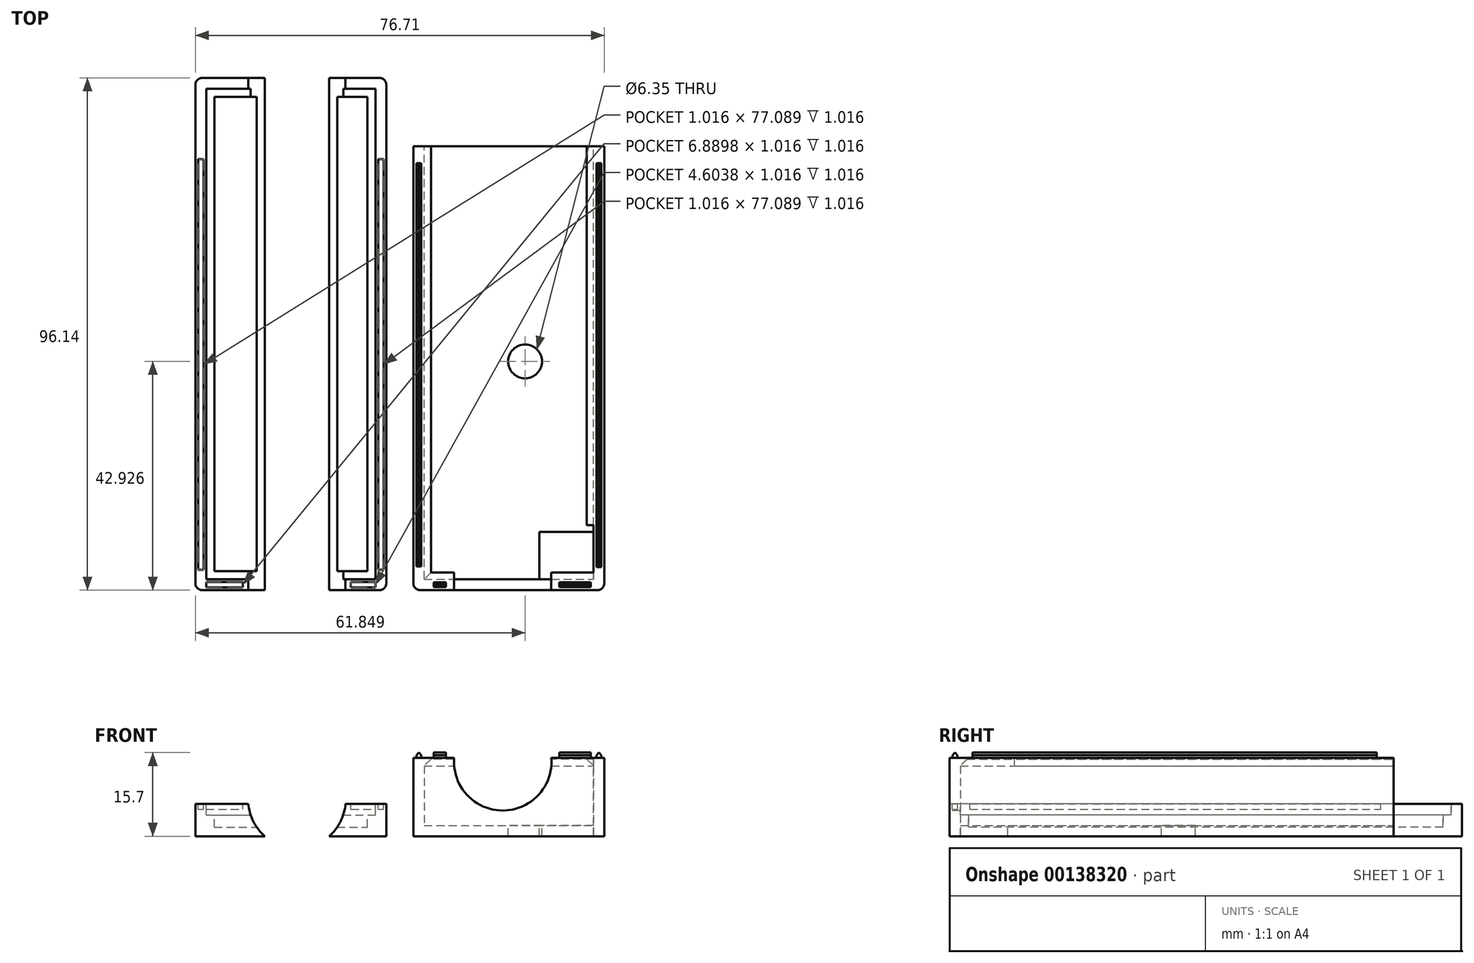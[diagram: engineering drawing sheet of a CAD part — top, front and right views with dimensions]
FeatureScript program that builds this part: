
annotation { "Feature Type Name" : "Feature", "Feature Type Description" : "" }
export const myFeature = defineFeature(function(context is Context, id is Id, definition is map)
    precondition{}
    {
        {
            var Q0;
            Q0=qCreatedBy(makeId("Top.planeOp"),FACE);
            var sketch = newSketch(context, id + "F0", { "sketchPlane" : qUnion([Q0])});
            skLineSegment(sketch, "E0.bottom", {"start": v(2.54, 98.68) * mm, "end": v(38.35, 98.68) * mm});
            skLineSegment(sketch, "E0.top", {"start": v(2.54, 2.54) * mm, "end": v(38.35, 2.54) * mm});
            skLineSegment(sketch, "E0.left", {"start": v(2.54, 98.68) * mm, "end": v(2.54, 2.54) * mm});
            skLineSegment(sketch, "E0.right", {"start": v(38.35, 98.68) * mm, "end": v(38.35, 2.54) * mm});
            skSolve(sketch);
        }
        {
            var Q0;
            Q0 = qSketchRegion(id + "F0", true);
            extrude(context, id + "F1", {"entities" : qUnion([Q0]), "depth" : 6.1 * mm, "offsetDistance" : 25.4 * mm});
        }
        {
            var Q0;
            Q0=makeQuery(id+"F1.opExtrude","CAP_FACE",FACE,{"disambiguationData":[OSD([sQuery(id+"F0.wireOp",EDGE,"E0.bottom"),sQuery(id+"F0.wireOp",EDGE,"E0.top"),sQuery(id+"F0.wireOp",EDGE,"E0.left"),sQuery(id+"F0.wireOp",EDGE,"E0.right")])],"isStart":false});
            var sketch = newSketch(context, id + "F2", { "sketchPlane" : qUnion([Q0])});
            skLineSegment(sketch, "E1.0", {"start": v(34.8, 95.12) * mm, "end": v(34.8, 6.1) * mm});
            skLineSegment(sketch, "E1.1", {"start": v(6.1, 95.12) * mm, "end": v(34.8, 95.12) * mm});
            skLineSegment(sketch, "E1.2", {"start": v(6.1, 95.12) * mm, "end": v(6.1, 6.1) * mm});
            skLineSegment(sketch, "E1.3", {"start": v(6.1, 6.1) * mm, "end": v(34.8, 6.1) * mm});
            skSolve(sketch);
        }
        {
            var Q0;
            Q0 = qSketchRegion(id + "F2", true);
            extrude(context, id + "F3", {"entities" : qUnion([Q0]), "operationType" : NewBodyOperationType.REMOVE, "oppositeDirection" : true, "depth" : 4.4 * mm, "offsetDistance" : 25.4 * mm});
        }
        {
            var Q0;
            Q0=makeQuery(id+"F1.opExtrude","CAP_FACE",FACE,{"disambiguationData":[OSD([sQuery(id+"F0.wireOp",EDGE,"E0.bottom"),sQuery(id+"F0.wireOp",EDGE,"E0.top"),sQuery(id+"F0.wireOp",EDGE,"E0.left"),sQuery(id+"F0.wireOp",EDGE,"E0.right")])],"isStart":false});
            var sketch = newSketch(context, id + "F4", { "sketchPlane" : qUnion([Q0])});
            skLineSegment(sketch, "E2.0", {"start": v(4.57, 96.65) * mm, "end": v(4.57, 4.57) * mm});
            skLineSegment(sketch, "E2.1", {"start": v(4.57, 96.65) * mm, "end": v(36.32, 96.65) * mm});
            skLineSegment(sketch, "E2.2", {"start": v(36.32, 96.65) * mm, "end": v(36.32, 4.57) * mm});
            skLineSegment(sketch, "E2.3", {"start": v(4.57, 4.57) * mm, "end": v(36.32, 4.57) * mm});
            skLineSegment(sketch, "E3.bottom", {"start": v(6.1, 6.1) * mm, "end": v(34.8, 6.1) * mm});
            skLineSegment(sketch, "E3.top", {"start": v(6.1, 95.12) * mm, "end": v(34.8, 95.12) * mm});
            skLineSegment(sketch, "E3.left", {"start": v(6.1, 6.1) * mm, "end": v(6.1, 95.12) * mm});
            skLineSegment(sketch, "E3.right", {"start": v(34.8, 6.1) * mm, "end": v(34.8, 95.12) * mm});
            skSolve(sketch);
        }
        {
            var Q0;
            Q0 = qSketchRegion(id + "F4", true);
            extrude(context, id + "F5", {"entities" : qUnion([Q0]), "operationType" : NewBodyOperationType.REMOVE, "oppositeDirection" : true, "depth" : 2.1 * mm, "offsetDistance" : 25.4 * mm});
        }
        {
            var Q0;
            Q0=qCreatedBy(makeId("Top.planeOp"),FACE);
            var sketch = newSketch(context, id + "F6", { "sketchPlane" : qUnion([Q0])});
            skLineSegment(sketch, "E4.bottom", {"start": v(43.43, 2.54) * mm, "end": v(79.25, 2.54) * mm});
            skLineSegment(sketch, "E4.top", {"start": v(43.43, 98.55) * mm, "end": v(79.25, 98.55) * mm});
            skLineSegment(sketch, "E4.left", {"start": v(43.43, 2.54) * mm, "end": v(43.43, 98.55) * mm});
            skLineSegment(sketch, "E4.right", {"start": v(79.25, 2.54) * mm, "end": v(79.25, 98.55) * mm});
            skSolve(sketch);
        }
        {
            var Q0;
            Q0 = qSketchRegion(id + "F6", true);
            extrude(context, id + "F7", {"entities" : qUnion([Q0]), "depth" : 14.73 * mm, "offsetDistance" : 25.4 * mm});
        }
        {
            var Q0;
            Q0=makeQuery(id+"F7.opExtrude","CAP_FACE",FACE,{"disambiguationData":[OSD([sQuery(id+"F6.wireOp",EDGE,"E4.bottom"),sQuery(id+"F6.wireOp",EDGE,"E4.top"),sQuery(id+"F6.wireOp",EDGE,"E4.left"),sQuery(id+"F6.wireOp",EDGE,"E4.right")])],"isStart":false});
            shell(context, id + "F8", {"entities" : qUnion([Q0]), "thickness" : 2.03 * mm});
        }
        {
            var Q0;
            Q0=makeQuery(id+"F7.opExtrude","CAP_FACE",FACE,{"disambiguationData":[OSD([sQuery(id+"F6.wireOp",EDGE,"E4.bottom"),sQuery(id+"F6.wireOp",EDGE,"E4.top"),sQuery(id+"F6.wireOp",EDGE,"E4.left"),sQuery(id+"F6.wireOp",EDGE,"E4.right")])],"isStart":false});
            var sketch = newSketch(context, id + "F9", { "sketchPlane" : qUnion([Q0])});
            skLineSegment(sketch, "E5.bottom", {"start": v(43.43, 98.55) * mm, "end": v(79.25, 98.55) * mm});
            skLineSegment(sketch, "E5.top", {"start": v(43.43, 85.85) * mm, "end": v(79.25, 85.85) * mm});
            skLineSegment(sketch, "E5.left", {"start": v(43.43, 98.55) * mm, "end": v(43.43, 85.85) * mm});
            skLineSegment(sketch, "E5.right", {"start": v(79.25, 98.55) * mm, "end": v(79.25, 85.85) * mm});
            skLineSegment(sketch, "E6.bottom", {"start": v(77.22, 4.57) * mm, "end": v(67.06, 4.57) * mm});
            skLineSegment(sketch, "E6.top", {"start": v(77.22, 13.46) * mm, "end": v(67.06, 13.46) * mm});
            skLineSegment(sketch, "E6.left", {"start": v(77.22, 4.57) * mm, "end": v(77.22, 13.46) * mm});
            skLineSegment(sketch, "E6.right", {"start": v(67.06, 4.57) * mm, "end": v(67.06, 13.46) * mm});
            skCircle(sketch, "E7", {"center": v(64.39, 45.47) * mm, "radius": 3.18 * mm});
            skSolve(sketch);
        }
        {
            var Q0;
            Q0 = qSketchRegion(id + "F9", true);
            extrude(context, id + "F10", {"entities" : qUnion([Q0]), "operationType" : NewBodyOperationType.REMOVE, "endBound" : BoundingType.THROUGH_ALL, "oppositeDirection" : true, "depth" : 25.4 * mm, "offsetDistance" : 25.4 * mm});
        }
        {
            var Q0;
            {var subQ0=sQuery(id+"F6.wireOp",EDGE,"E4.bottom");var subQ1=sQuery(id+"F6.wireOp",EDGE,"E4.right");Q0=makeQuery(id+"F10.boolean.opBoolean","SPLIT",FACE,{"disambiguationData":[TD([makeQuery(id+"F7.opExtrude","SWEPT_FACE",FACE,{"disambiguationData":[OSD([subQ1])]})])],"derivedFrom":makeQuery(id+"F7.opExtrude","CAP_FACE",FACE,{"disambiguationData":[OSD([subQ0,sQuery(id+"F6.wireOp",EDGE,"E4.top"),sQuery(id+"F6.wireOp",EDGE,"E4.left"),subQ1])],"isStart":false})});}
            var sketch = newSketch(context, id + "F11", { "sketchPlane" : qUnion([Q0])});
            skLineSegment(sketch, "E8.bottom", {"start": v(77.22, 14.73) * mm, "end": v(75.95, 14.73) * mm});
            skLineSegment(sketch, "E8.top", {"start": v(77.22, 85.85) * mm, "end": v(75.95, 85.85) * mm});
            skLineSegment(sketch, "E8.left", {"start": v(77.22, 14.73) * mm, "end": v(77.22, 85.85) * mm});
            skLineSegment(sketch, "E8.right", {"start": v(75.95, 14.73) * mm, "end": v(75.95, 85.85) * mm});
            skLineSegment(sketch, "E9.bottom", {"start": v(45.47, 4.57) * mm, "end": v(77.22, 4.57) * mm});
            skLineSegment(sketch, "E9.top", {"start": v(46.74, 5.84) * mm, "end": v(77.22, 5.84) * mm});
            skLineSegment(sketch, "E9.right", {"start": v(77.22, 4.57) * mm, "end": v(77.22, 5.84) * mm});
            skLineSegment(sketch, "E10.top", {"start": v(46.74, 85.85) * mm, "end": v(45.47, 85.85) * mm});
            skLineSegment(sketch, "E10.left", {"start": v(46.74, 5.84) * mm, "end": v(46.74, 85.85) * mm});
            skLineSegment(sketch, "E10.right", {"start": v(45.47, 4.57) * mm, "end": v(45.47, 85.85) * mm});
            skSolve(sketch);
        }
        {
            var Q0;
            Q0 = qSketchRegion(id + "F11", true);
            extrude(context, id + "F12", {"entities" : qUnion([Q0]), "operationType" : NewBodyOperationType.ADD, "oppositeDirection" : true, "depth" : 1.52 * mm, "offsetDistance" : 25.4 * mm});
        }
        {
            var Q0;
            Q0=makeQuery(id+"F12.opExtrude","CAP_EDGE",EDGE,{"disambiguationData":[OSD([sQuery(id+"F11.wireOp",EDGE,"E9.top")])],"isStart":false});
            var Q1;
            Q1=makeQuery(id+"F12.opExtrude","CAP_EDGE",EDGE,{"disambiguationData":[OSD([sQuery(id+"F11.wireOp",EDGE,"E8.right")])],"isStart":false});
            var Q2;
            Q2=makeQuery(id+"F12.opExtrude","CAP_EDGE",EDGE,{"disambiguationData":[OSD([sQuery(id+"F11.wireOp",EDGE,"E10.left")])],"isStart":false});
            var Q3;
            Q3=makeQuery(id+"F12.opExtrude","CAP_EDGE",EDGE,{"disambiguationData":[OSD([sQuery(id+"F11.wireOp",EDGE,"Zw6snLi4-Jf5f-Ahn4-wR1g-vWgNg3NE2vRn.top")])],"isStart":false});
            chamfer(context, id + "F13", {"entities" : qUnion([Q0, Q1, Q2, Q3]), "width" : 1.27 * mm, "tangentPropagation" : true});
        }
        {
            var Q0;
            Q0=makeQuery(id+"F7.opExtrude","SWEPT_EDGE",EDGE,{"disambiguationData":[OSD([sQuery(id+"F6.wireOp",EDGE,"E4.bottom"),sQuery(id+"F6.wireOp",EDGE,"E4.right")])]});
            var Q1;
            Q1=makeQuery(id+"F7.opExtrude","SWEPT_EDGE",EDGE,{"disambiguationData":[OSD([sQuery(id+"F6.wireOp",EDGE,"E4.bottom"),sQuery(id+"F6.wireOp",EDGE,"E4.left")])]});
            var Q2;
            Q2=makeQuery(id+"F1.opExtrude","SWEPT_EDGE",EDGE,{"disambiguationData":[OSD([sQuery(id+"F0.wireOp",EDGE,"E0.top"),sQuery(id+"F0.wireOp",EDGE,"E0.right")])]});
            var Q3;
            Q3=makeQuery(id+"F1.opExtrude","SWEPT_EDGE",EDGE,{"disambiguationData":[OSD([sQuery(id+"F0.wireOp",EDGE,"E0.bottom"),sQuery(id+"F0.wireOp",EDGE,"E0.right")])]});
            var Q4;
            Q4=makeQuery(id+"F1.opExtrude","SWEPT_EDGE",EDGE,{"disambiguationData":[OSD([sQuery(id+"F0.wireOp",EDGE,"E0.top"),sQuery(id+"F0.wireOp",EDGE,"E0.left")])]});
            var Q5;
            Q5=makeQuery(id+"F1.opExtrude","SWEPT_EDGE",EDGE,{"disambiguationData":[OSD([sQuery(id+"F0.wireOp",EDGE,"E0.bottom"),sQuery(id+"F0.wireOp",EDGE,"E0.left")])]});
            fillet(context, id + "F14", {"entities" : qUnion([Q0, Q1, Q2, Q3, Q4, Q5]), "tangentPropagation" : true, "radius" : 1.27 * mm, "defaultsChanged" : false, "vertexSettings" : [], "allowEdgeOverflow" : false});
        }
        {
            var Q0;
            Q0=makeQuery(id+"F7.opExtrude","SWEPT_FACE",FACE,{"disambiguationData":[OSD([sQuery(id+"F6.wireOp",EDGE,"E4.bottom")])]});
            var sketch = newSketch(context, id + "F15", { "sketchPlane" : qUnion([Q0])});
            skCircle(sketch, "E11", {"center": v(60.2, 13.97) * mm, "radius": 9.14 * mm});
            skPoint(sketch, "E11.centerSnap0", {"position": v(61.34, 14.73) * mm});
            skCircle(sketch, "E12", {"center": v(21.59, 6.86) * mm, "radius": 9.14 * mm});
            skSolve(sketch);
        }
        {
            var Q0;
            Q0 = qSketchRegion(id + "F15", true);
            extrude(context, id + "F16", {"entities" : qUnion([Q0]), "operationType" : NewBodyOperationType.REMOVE, "endBound" : BoundingType.THROUGH_ALL, "oppositeDirection" : true, "depth" : 25.4 * mm, "offsetDistance" : 25.4 * mm});
        }
        {
            var Q0;
            Q0 = qSketchRegion(id + "F15", true);
            extrude(context, id + "F17", {"entities" : qUnion([Q0]), "operationType" : NewBodyOperationType.REMOVE, "oppositeDirection" : true, "depth" : 3.56 * mm, "offsetDistance" : 25.4 * mm});
        }
        {
            var Q0;
            Q0=makeQuery(id+"F1.opExtrude","CAP_FACE",FACE,{"disambiguationData":[OSD([sQuery(id+"F0.wireOp",EDGE,"E0.bottom"),sQuery(id+"F0.wireOp",EDGE,"E0.top"),sQuery(id+"F0.wireOp",EDGE,"E0.left"),sQuery(id+"F0.wireOp",EDGE,"E0.right")])],"isStart":false});
            var sketch = newSketch(context, id + "F18", { "sketchPlane" : qUnion([Q0])});
            skLineSegment(sketch, "E13.bottom", {"start": v(4.57, 3.05) * mm, "end": v(11.46, 3.05) * mm});
            skLineSegment(sketch, "E13.top", {"start": v(4.57, 4.06) * mm, "end": v(11.46, 4.06) * mm});
            skLineSegment(sketch, "E13.left", {"start": v(4.57, 3.05) * mm, "end": v(4.57, 4.06) * mm});
            skLineSegment(sketch, "E13.right", {"start": v(11.46, 3.05) * mm, "end": v(11.46, 4.06) * mm});
            skLineSegment(sketch, "E14.bottom", {"start": v(3.05, 6.35) * mm, "end": v(4.06, 6.35) * mm});
            skLineSegment(sketch, "E14.top", {"start": v(3.05, 83.44) * mm, "end": v(4.06, 83.44) * mm});
            skLineSegment(sketch, "E14.left", {"start": v(3.05, 6.35) * mm, "end": v(3.05, 83.44) * mm});
            skLineSegment(sketch, "E14.right", {"start": v(4.06, 6.35) * mm, "end": v(4.06, 83.44) * mm});
            skLineSegment(sketch, "E15.bottom", {"start": v(36.83, 6.35) * mm, "end": v(37.85, 6.35) * mm});
            skLineSegment(sketch, "E15.top", {"start": v(36.83, 83.44) * mm, "end": v(37.85, 83.44) * mm});
            skLineSegment(sketch, "E15.left", {"start": v(36.83, 6.35) * mm, "end": v(36.83, 83.44) * mm});
            skLineSegment(sketch, "E15.right", {"start": v(37.85, 6.35) * mm, "end": v(37.85, 83.44) * mm});
            skLineSegment(sketch, "E16.bottom", {"start": v(31.72, 3.05) * mm, "end": v(36.32, 3.05) * mm});
            skLineSegment(sketch, "E16.top", {"start": v(31.72, 4.06) * mm, "end": v(36.32, 4.06) * mm});
            skLineSegment(sketch, "E16.left", {"start": v(31.72, 3.05) * mm, "end": v(31.72, 4.06) * mm});
            skLineSegment(sketch, "E16.right", {"start": v(36.32, 3.05) * mm, "end": v(36.32, 4.06) * mm});
            skSolve(sketch);
        }
        {
            var Q0;
            Q0 = qSketchRegion(id + "F18", true);
            extrude(context, id + "F19", {"entities" : qUnion([Q0]), "operationType" : NewBodyOperationType.REMOVE, "oppositeDirection" : true, "depth" : 1.02 * mm, "offsetDistance" : 25.4 * mm});
        }
        {
            var Q0;
            {var subQ0=sQuery(id+"F11.wireOp",EDGE,"E8.top");var subQ1=sQuery(id+"F6.wireOp",EDGE,"E4.bottom");var subQ2=sQuery(id+"F11.wireOp",EDGE,"E10.left");var subQ3=sQuery(id+"F6.wireOp",EDGE,"E4.left");var subQ4=sQuery(id+"F11.wireOp",EDGE,"E9.top");var subQ5=sQuery(id+"F11.wireOp",EDGE,"E10.top");Q0=makeQuery(id+"F16.boolean.opBoolean","SPLIT",FACE,{"disambiguationData":[TD([makeQuery(id+"F7.opExtrude","SWEPT_FACE",FACE,{"disambiguationData":[OSD([subQ3])]})])],"derivedFrom":makeQuery(id+"F12.boolean.opBoolean","MERGE",FACE,{"derivedFrom":[makeQuery(id+"F7.opExtrude","CAP_FACE",FACE,{"disambiguationData":[OSD([subQ1,sQuery(id+"F6.wireOp",EDGE,"E4.top"),subQ3,sQuery(id+"F6.wireOp",EDGE,"E4.right")])],"isStart":false}),makeQuery(id+"F12.opExtrude","CAP_FACE",FACE,{"disambiguationData":[OSD([sQuery(id+"F11.wireOp",EDGE,"E8.bottom"),subQ0,sQuery(id+"F11.wireOp",EDGE,"E8.left"),sQuery(id+"F11.wireOp",EDGE,"E8.right")])],"isStart":true}),makeQuery(id+"F12.opExtrude","CAP_FACE",FACE,{"disambiguationData":[OSD([sQuery(id+"F11.wireOp",EDGE,"E9.bottom"),subQ4,sQuery(id+"F11.wireOp",EDGE,"E9.right"),subQ5,subQ2,sQuery(id+"F11.wireOp",EDGE,"E10.right")])],"isStart":true})]})});}
            var sketch = newSketch(context, id + "F20", { "sketchPlane" : qUnion([Q0])});
            skLineSegment(sketch, "E17.bottom", {"start": v(47.24, 4.01) * mm, "end": v(49.56, 4.01) * mm});
            skLineSegment(sketch, "E17.top", {"start": v(47.24, 3.1) * mm, "end": v(49.56, 3.1) * mm});
            skLineSegment(sketch, "E17.left", {"start": v(47.24, 4.01) * mm, "end": v(47.24, 3.1) * mm});
            skLineSegment(sketch, "E17.right", {"start": v(49.56, 4.01) * mm, "end": v(49.56, 3.1) * mm});
            skLineSegment(sketch, "E18.bottom", {"start": v(44, 6.99) * mm, "end": v(44.9, 6.99) * mm});
            skLineSegment(sketch, "E18.top", {"start": v(44, 82.68) * mm, "end": v(44.9, 82.68) * mm});
            skLineSegment(sketch, "E18.left", {"start": v(44, 6.99) * mm, "end": v(44, 82.68) * mm});
            skLineSegment(sketch, "E18.right", {"start": v(44.9, 6.99) * mm, "end": v(44.9, 82.68) * mm});
            skLineSegment(sketch, "E19.bottom", {"start": v(70.83, 3.1) * mm, "end": v(76.7, 3.1) * mm});
            skLineSegment(sketch, "E19.top", {"start": v(70.83, 4.01) * mm, "end": v(76.7, 4.01) * mm});
            skLineSegment(sketch, "E19.left", {"start": v(70.83, 3.1) * mm, "end": v(70.83, 4.01) * mm});
            skLineSegment(sketch, "E19.right", {"start": v(76.7, 3.1) * mm, "end": v(76.7, 4.01) * mm});
            skLineSegment(sketch, "E20.bottom", {"start": v(77.77, 6.86) * mm, "end": v(78.69, 6.86) * mm});
            skLineSegment(sketch, "E20.top", {"start": v(77.77, 82.68) * mm, "end": v(78.69, 82.68) * mm});
            skLineSegment(sketch, "E20.left", {"start": v(77.77, 6.86) * mm, "end": v(77.77, 82.68) * mm});
            skLineSegment(sketch, "E20.right", {"start": v(78.69, 6.86) * mm, "end": v(78.69, 82.68) * mm});
            skSolve(sketch);
        }
        {
            var Q0;
            Q0 = qSketchRegion(id + "F20", true);
            extrude(context, id + "F21", {"entities" : qUnion([Q0]), "operationType" : NewBodyOperationType.ADD, "depth" : 1.14 * mm, "offsetDistance" : 25.4 * mm});
        }
        {
            var Q0;
            Q0=makeQuery(id+"F21.opExtrude","CAP_EDGE",EDGE,{"disambiguationData":[OSD([sQuery(id+"F20.wireOp",EDGE,"E17.top")])],"isStart":false});
            var Q1;
            Q1=makeQuery(id+"F21.opExtrude","CAP_EDGE",EDGE,{"disambiguationData":[OSD([sQuery(id+"F20.wireOp",EDGE,"E17.bottom")])],"isStart":false});
            var Q2;
            Q2=makeQuery(id+"F21.opExtrude","CAP_EDGE",EDGE,{"disambiguationData":[OSD([sQuery(id+"F20.wireOp",EDGE,"E18.right")])],"isStart":false});
            var Q3;
            Q3=makeQuery(id+"F21.opExtrude","CAP_EDGE",EDGE,{"disambiguationData":[OSD([sQuery(id+"F20.wireOp",EDGE,"E18.left")])],"isStart":false});
            var Q4;
            Q4=makeQuery(id+"F21.opExtrude","CAP_EDGE",EDGE,{"disambiguationData":[OSD([sQuery(id+"F20.wireOp",EDGE,"E19.bottom")])],"isStart":false});
            var Q5;
            Q5=makeQuery(id+"F21.opExtrude","CAP_EDGE",EDGE,{"disambiguationData":[OSD([sQuery(id+"F20.wireOp",EDGE,"E19.top")])],"isStart":false});
            var Q6;
            Q6=makeQuery(id+"F21.opExtrude","CAP_EDGE",EDGE,{"disambiguationData":[OSD([sQuery(id+"F20.wireOp",EDGE,"E20.right")])],"isStart":false});
            var Q7;
            Q7=makeQuery(id+"F21.opExtrude","CAP_EDGE",EDGE,{"disambiguationData":[OSD([sQuery(id+"F20.wireOp",EDGE,"E20.left")])],"isStart":false});
            chamfer(context, id + "F22", {"entities" : qUnion([Q0, Q1, Q2, Q3, Q4, Q5, Q6, Q7]), "width" : 0.64 * mm, "tangentPropagation" : true});
        }
    });
